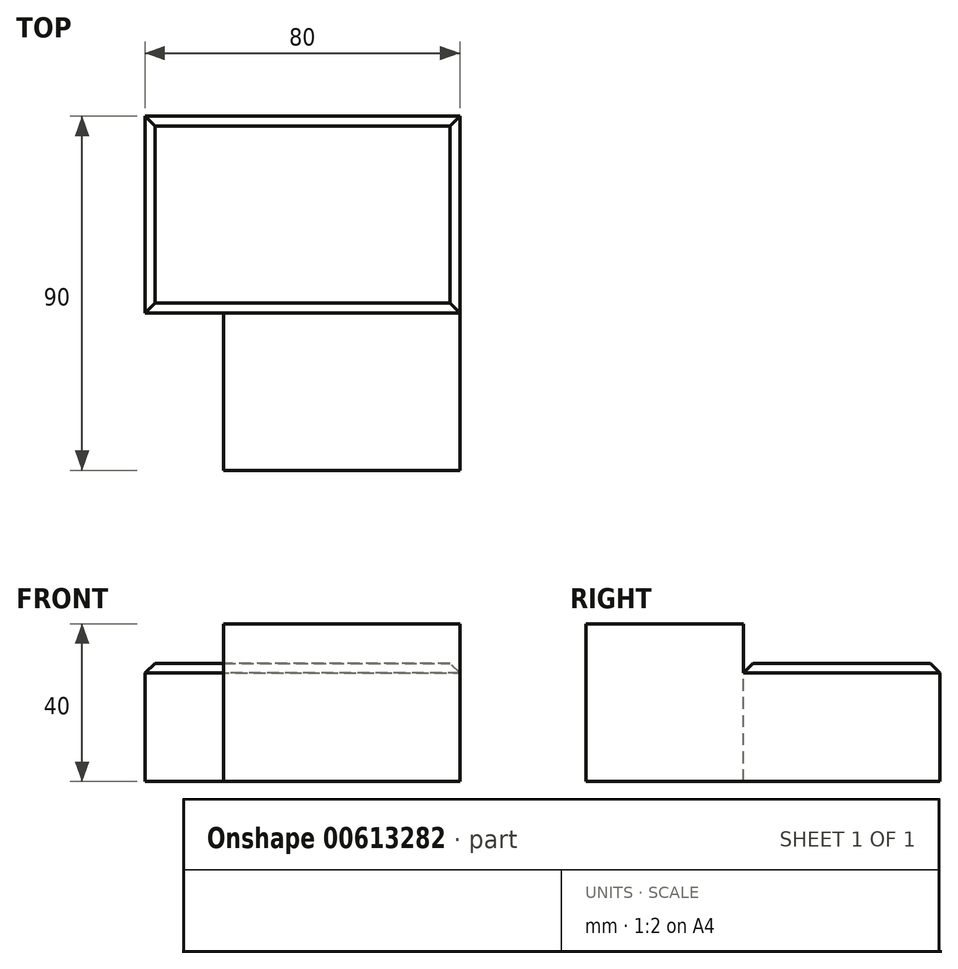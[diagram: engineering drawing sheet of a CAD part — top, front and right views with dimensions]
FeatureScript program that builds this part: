
annotation { "Feature Type Name" : "Feature", "Feature Type Description" : "" }
export const myFeature = defineFeature(function(context is Context, id is Id, definition is map)
    precondition{}
    {
        {
            var Q0;
            Q0=qCreatedBy(makeId("Top.planeOp"),FACE);
            var sketch = newSketch(context, id + "F0", { "sketchPlane" : qUnion([Q0])});
            skLineSegment(sketch, "E0.bottom", {"start": v(0, 0) * mm, "end": v(-80, 0) * mm});
            skLineSegment(sketch, "E0.top", {"start": v(0, -50) * mm, "end": v(-80, -50) * mm});
            skLineSegment(sketch, "E0.left", {"start": v(0, 0) * mm, "end": v(0, -50) * mm});
            skLineSegment(sketch, "E0.right", {"start": v(-80, 0) * mm, "end": v(-80, -50) * mm});
            skSolve(sketch);
        }
        {
            var Q0;
            Q0 = qSketchRegion(id + "F0", true);
            extrude(context, id + "F1", {"entities" : qUnion([Q0]), "depth" : 30 * mm, "offsetDistance" : 25 * mm});
        }
        {
            var Q0;
            Q0=makeQuery(id+"F1.opExtrude","CAP_FACE",FACE,{"disambiguationData":[OSD([sQuery(id+"F0.wireOp",EDGE,"E0.bottom"),sQuery(id+"F0.wireOp",EDGE,"E0.top"),sQuery(id+"F0.wireOp",EDGE,"E0.left"),sQuery(id+"F0.wireOp",EDGE,"E0.right")])],"isStart":false});
            chamfer(context, id + "F2", {"entities" : qUnion([Q0]), "width" : 2.5 * mm, "tangentPropagation" : true});
        }
        {
            var Q0;
            Q0=makeQuery(id+"F1.opExtrude","SWEPT_FACE",FACE,{"disambiguationData":[OSD([sQuery(id+"F0.wireOp",EDGE,"E0.top")])]});
            var sketch = newSketch(context, id + "F3", { "sketchPlane" : qUnion([Q0])});
            skLineSegment(sketch, "E1.bottom", {"start": v(0, 0) * mm, "end": v(-60, 0) * mm});
            skLineSegment(sketch, "E1.top", {"start": v(0, 40) * mm, "end": v(-60, 40) * mm});
            skLineSegment(sketch, "E1.left", {"start": v(0, 0) * mm, "end": v(0, 40) * mm});
            skLineSegment(sketch, "E1.right", {"start": v(-60, 0) * mm, "end": v(-60, 40) * mm});
            skSolve(sketch);
        }
        {
            var Q0;
            Q0 = qSketchRegion(id + "F3", true);
            extrude(context, id + "F4", {"entities" : qUnion([Q0]), "operationType" : NewBodyOperationType.ADD, "depth" : 40 * mm, "offsetDistance" : 25 * mm});
        }
    });
